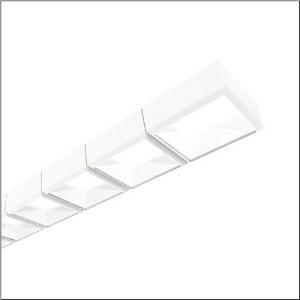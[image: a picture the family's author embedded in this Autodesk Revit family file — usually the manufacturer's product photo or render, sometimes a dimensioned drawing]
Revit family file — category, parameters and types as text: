
# Revit family: scriptus_r__11_5mz312d04wa_0fc2
name_source: partatom
category: Lighting Fixtures
units: mm (PartAtom-declared; Revit-internal decimal feet)

## family parameters
Cut with Voids When Loaded = No
Host = Face
Light Source = No
Part Type = Normal
Room Calculation Point = No
Round Connector Dimension = Use Diameter
Shared = No

## types (1)
- Scriptus® 11 (1 x LED 4000K / CRI = 80 (unbekannt), 1610 lm / 2410 lm, 4000K)
    Apparent Load = 62 VA
    CIE Flux Codes = - - - 0 100 / 82 95 99 100 100
    Color Rendering = 80
    Color Temperature = 4000K
    Default Elevation = 1800 mm
    Description = Scriptus® 11, office luminaire, primary optical cover: lenses, CAT 2 (L<= 3000cd/m²), light emission: direct/indirect distribution, primary light characteristic: symmetric, installation type: suspended mounting, LED rated luminous flux: 8.020 lm, light colour: 840, colour temperature: 4000K, control gear: ECG DALI, with terminal, 5-pole, mains connection: 230V, AC, 50Hz, rated input power: 62W, LED control gear: ECG DALI, housing, luminaire housing, of aluminium, traffic white (RAL 9016), length: 1.658 mm, width: 114 mm, height: 57mm, protection rating (complete): IP20, insulation class (complete): insulation class I (protective earthing), certification: CE, ENEC, VDE, protection symbol: F, permissible ambient temperature for indoor applications: 0..+35°C, standard: EN 50419, packaging unit: 1 piece
    Height = 57 mm
    Lamp = 1 x LED 4000K / CRI >= 80 (unbekannt)
    Lamp Light Flux = 1610 lm / 2410 lm
    Lamp count = 1
    Length = 1658 mm
    Luminous efficacy = 131 lm/W
    Manufacturer = Siteco
    ModVariant = No
    Model = 5MZ312D04WA
    Mounting Place = Ceiling
    Mounting Type = Pendant
    Number of Poles = 1
    OnlyDefault = Yes
    Power Factor = 1
    Product Name = Scriptus® 11
    Product group = office luminaire | ceiling pendant
    ProductGroupID = 905
    Protection Class = Protection class I
    Protection Degree = IP 20
    RLX_Detail_Level = 1
    RlxData = <blob elided: 31133 chars, md5=a54c9e15>
    Socket = socket
    Standby Power = 0 W
    System Light Flux = 8040 lm
    System Power = 62 W
    Type Comments = Product without accessories
    Type Image = l_1004839.jpg
    URL = http://relux.com
    VarID = ---
    Voltage = 0 V
    Weight = 0.00 kg
    Width = 114 mm

## geometry (parser evidence)
native form markers: Blend x4, Sweep x17
no freeform markers — native parametric forms only
